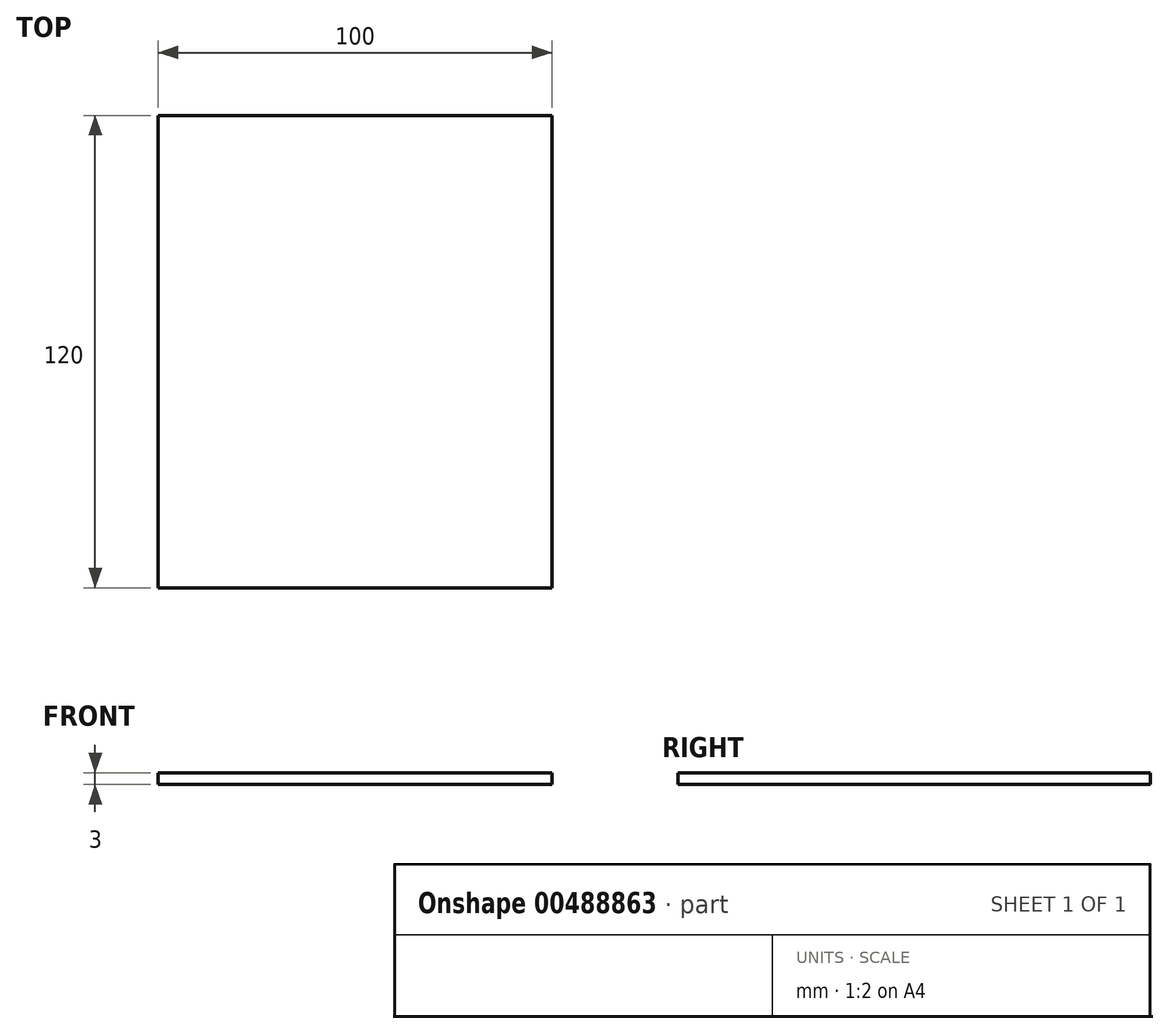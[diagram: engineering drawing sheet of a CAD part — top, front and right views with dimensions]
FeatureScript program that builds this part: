
annotation { "Feature Type Name" : "Feature", "Feature Type Description" : "" }
export const myFeature = defineFeature(function(context is Context, id is Id, definition is map)
    precondition{}
    {
        {
            var Q0;
            Q0=qCreatedBy(makeId("Top.planeOp"),FACE);
            var sketch = newSketch(context, id + "F0", { "sketchPlane" : qUnion([Q0])});
            skLineSegment(sketch, "E0.bottom", {"start": v(-56.5, 72.88) * mm, "end": v(43.5, 72.88) * mm});
            skLineSegment(sketch, "E0.top", {"start": v(-56.5, -47.12) * mm, "end": v(43.5, -47.12) * mm});
            skLineSegment(sketch, "E0.left", {"start": v(-56.5, 72.88) * mm, "end": v(-56.5, -47.12) * mm});
            skLineSegment(sketch, "E0.right", {"start": v(43.5, 72.88) * mm, "end": v(43.5, -47.12) * mm});
            skSolve(sketch);
        }
        {
            var Q0;
            Q0=makeQuery(id+"F0.imprint","IMPRINT",FACE,{"disambiguationData":[TD([[makeQuery(id+"F0.imprint","IMPRINT",EDGE,{"derivedFrom":sQuery(id+"F0.wireOp",EDGE,"E0.bottom")}),-1.0]])]});
            extrude(context, id + "F1", {"entities" : qUnion([Q0]), "depth" : 3 * mm});
        }
    });
